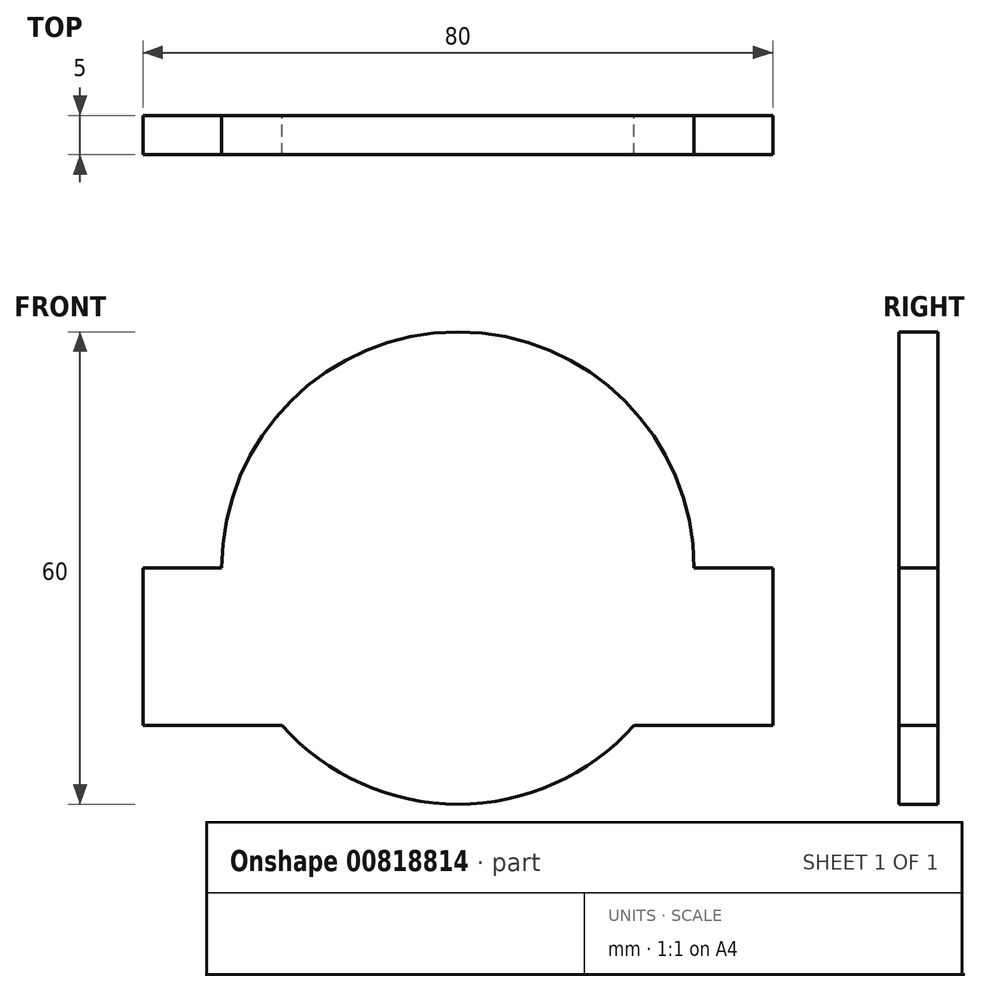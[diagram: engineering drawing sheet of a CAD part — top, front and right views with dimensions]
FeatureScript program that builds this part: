
annotation { "Feature Type Name" : "Feature", "Feature Type Description" : "" }
export const myFeature = defineFeature(function(context is Context, id is Id, definition is map)
    precondition{}
    {
        {
            var Q0;
            Q0=qCreatedBy(makeId("Front.planeOp"),FACE);
            var sketch = newSketch(context, id + "F0", { "sketchPlane" : qUnion([Q0])});
            skCircle(sketch, "E0", {"center": v(0, 0) * mm, "radius": 30 * mm});
            skLineSegment(sketch, "E1.bottom", {"start": v(40, 0) * mm, "end": v(-40, 0) * mm});
            skLineSegment(sketch, "E1.top", {"start": v(40, -20) * mm, "end": v(-40, -20) * mm});
            skLineSegment(sketch, "E1.left", {"start": v(40, 0) * mm, "end": v(40, -20) * mm});
            skLineSegment(sketch, "E1.right", {"start": v(-40, 0) * mm, "end": v(-40, -20) * mm});
            skPoint(sketch, "E1.middle", {"position": v(0, -10) * mm});
            skSolve(sketch);
        }
        {
            var Q0;
            Q0=qSketchRegion(id+"F0",true);
            extrude(context, id + "F1", {"entities" : qUnion([Q0]), "depth" : 5 * mm, "offsetDistance" : 25 * mm});
        }
    });
